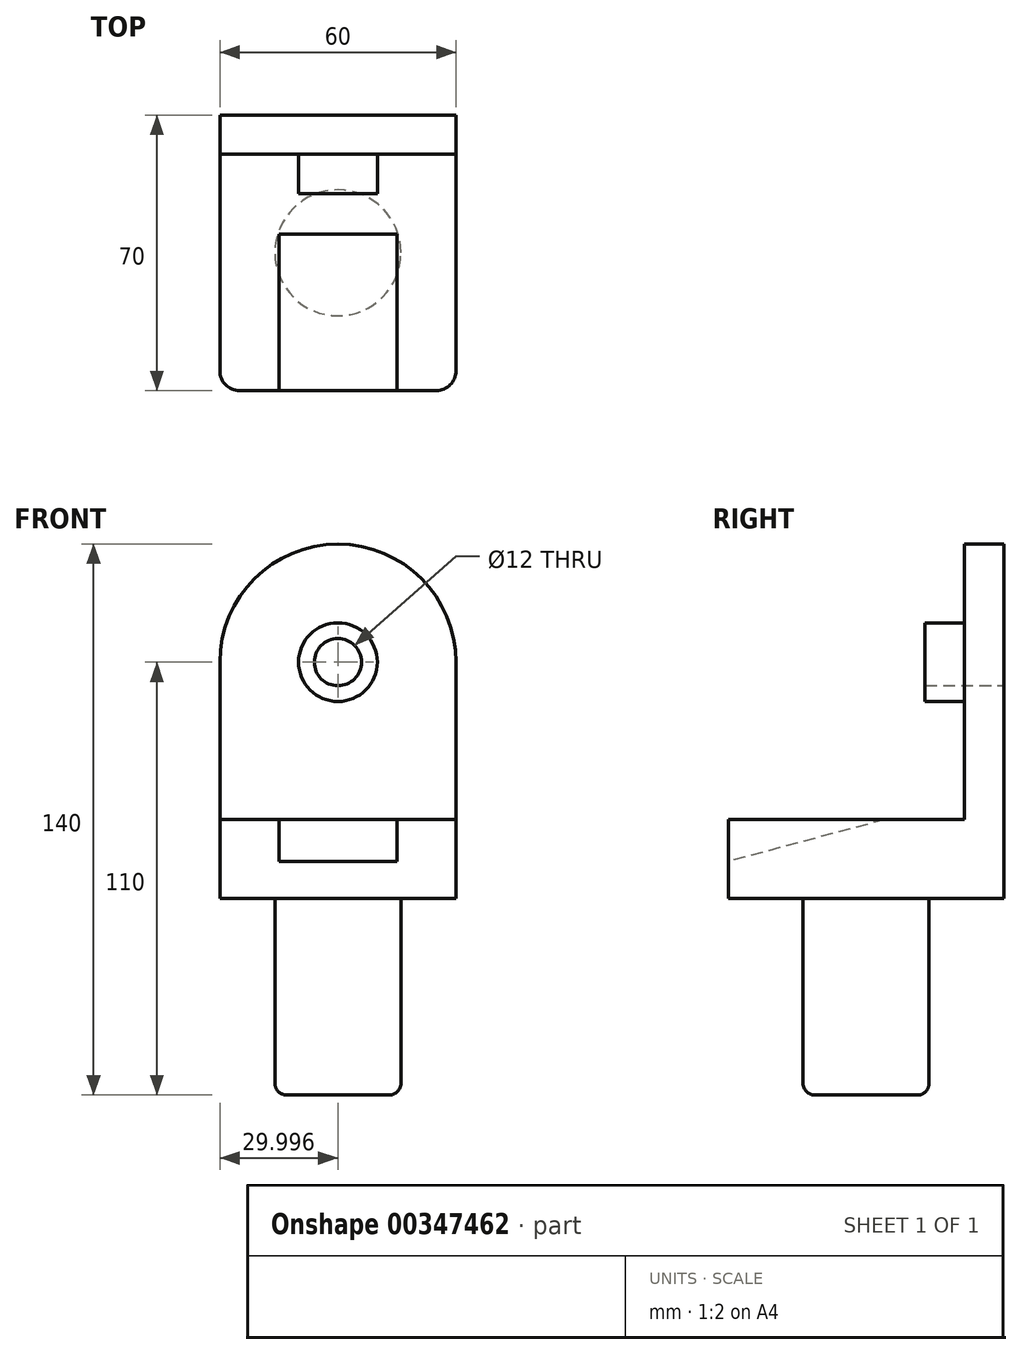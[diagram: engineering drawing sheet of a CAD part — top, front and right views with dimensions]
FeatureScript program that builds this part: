
annotation { "Feature Type Name" : "Feature", "Feature Type Description" : "" }
export const myFeature = defineFeature(function(context is Context, id is Id, definition is map)
    precondition{}
    {
        {
            var Q0;
            Q0=qCreatedBy(makeId("Top.planeOp"),FACE);
            var sketch = newSketch(context, id + "F0", { "sketchPlane" : qUnion([Q0])});
            skCircle(sketch, "E0", {"center": v(-41.77, 23.8) * mm, "radius": 16 * mm});
            skSolve(sketch);
        }
        {
            var Q0;
            Q0=makeQuery(id+"F0.imprint","IMPRINT",FACE,{"disambiguationData":[TD([[makeQuery(id+"F0.imprint","IMPRINT",EDGE,{"derivedFrom":sQuery(id+"F0.wireOp",EDGE,"E0")}),1.0]])]});
            extrude(context, id + "F1", {"entities" : qUnion([Q0]), "depth" : 50 * mm});
        }
        {
            var Q0;
            Q0=makeQuery(id+"F1.opExtrude","CAP_FACE",FACE,{"disambiguationData":[OSD([sQuery(id+"F0.wireOp",EDGE,"E0")])],"isStart":true});
            fillet(context, id + "F2", {"entities" : qUnion([Q0]), "radius" : 3 * mm, "tangentPropagation" : true, "allowEdgeOverflow" : false});
        }
        {
            var Q0;
            Q0=makeQuery(id+"F1.opExtrude","CAP_FACE",FACE,{"disambiguationData":[OSD([sQuery(id+"F0.wireOp",EDGE,"E0")])],"isStart":false});
            var sketch = newSketch(context, id + "F3", { "sketchPlane" : qUnion([Q0])});
            skLineSegment(sketch, "E1", {"start": v(-41.77, 58.8) * mm, "end": v(-71.77, 58.8) * mm});
            skLineSegment(sketch, "E2", {"start": v(-71.77, 58.8) * mm, "end": v(-71.77, 23.8) * mm});
            skLineSegment(sketch, "E3", {"start": v(-71.77, 23.8) * mm, "end": v(-71.77, -6.2) * mm});
            skLineSegment(sketch, "E4", {"start": v(-66.77, -11.2) * mm, "end": v(-16.77, -11.2) * mm});
            skLineSegment(sketch, "E5", {"start": v(-11.77, -6.2) * mm, "end": v(-11.77, 58.8) * mm});
            skLineSegment(sketch, "E6", {"start": v(-11.77, 58.8) * mm, "end": v(-41.77, 58.8) * mm});
            skPoint(sketch, "E7.visualSharp", {"position": v(-71.77, -11.2) * mm});
            skArc(sketch, "E7.filletArc", {"start": v(-71.77, -6.2) * mm, "mid": v(-70.3, -9.73) * mm, "end": v(-66.77, -11.2) * mm});
            skPoint(sketch, "E8.visualSharp", {"position": v(-11.77, -11.2) * mm});
            skArc(sketch, "E8.filletArc", {"start": v(-16.77, -11.2) * mm, "mid": v(-13.24, -9.73) * mm, "end": v(-11.77, -6.2) * mm});
            skLineSegment(sketch, "E9", {"start": v(-41.77, -11.2) * mm, "end": v(-56.77, -11.2) * mm});
            skLineSegment(sketch, "E10", {"start": v(-41.77, -11.2) * mm, "end": v(-26.77, -11.2) * mm});
            skSolve(sketch);
        }
        {
            var Q0;
            Q0=makeQuery(id+"F3.imprint","IMPRINT",FACE,{"disambiguationData":[TD([[makeQuery(id+"F3.imprint","IMPRINT",EDGE,{"derivedFrom":makeQuery(id+"F1.opExtrude","CAP_EDGE",EDGE,{"disambiguationData":[OSD([sQuery(id+"F0.wireOp",EDGE,"E0")])],"isStart":false})}),1.0]])]});
            var Q1;
            Q1=makeQuery(id+"F3.imprint","IMPRINT",FACE,{"disambiguationData":[TD([[makeQuery(id+"F3.imprint","IMPRINT",EDGE,{"derivedFrom":sQuery(id+"F3.wireOp",EDGE,"E1")}),1.0]])]});
            extrude(context, id + "F4", {"entities" : qUnion([Q0, Q1]), "operationType" : NewBodyOperationType.ADD, "depth" : 20 * mm});
        }
        {
            var Q0;
            Q0=makeQuery(id+"F4.opExtrude","SWEPT_FACE",FACE,{"disambiguationData":[OSD([sQuery(id+"F3.wireOp",EDGE,"E2"),sQuery(id+"F3.wireOp",EDGE,"E3")])]});
            cPlane(context, id + "F5", {"entities" : qUnion([Q0]), "cplaneType" : CPlaneType.OFFSET, "offset" : 30 * mm, "oppositeDirection" : true, "width" : 150 * mm, "height" : 150 * mm});
        }
        {
            var Q0;
            Q0=qCreatedBy(id+"F5.planeOp",FACE);
            var sketch = newSketch(context, id + "F6", { "sketchPlane" : qUnion([Q0])});
            skLineSegment(sketch, "E11", {"start": v(11.26, 70.05) * mm, "end": v(-28.74, 70.05) * mm});
            skLineSegment(sketch, "E12", {"start": v(-28.74, 70.05) * mm, "end": v(11.26, 59.33) * mm});
            skLineSegment(sketch, "E13", {"start": v(11.26, 59.33) * mm, "end": v(11.26, 70.05) * mm});
            skSolve(sketch);
        }
        {
            var Q0;
            Q0 = qSketchRegion(id + "F6", true);
            extrude(context, id + "F7", {"entities" : qUnion([Q0]), "operationType" : NewBodyOperationType.REMOVE, "endBound" : BoundingType.SYMMETRIC, "oppositeDirection" : true, "depth" : 30 * mm});
        }
        {
            var Q0;
            Q0=makeQuery(id+"F4.opExtrude","CAP_FACE",FACE,{"disambiguationData":[OSD([sQuery(id+"F3.wireOp",EDGE,"E1"),sQuery(id+"F3.wireOp",EDGE,"E2"),sQuery(id+"F3.wireOp",EDGE,"E3"),sQuery(id+"F3.wireOp",EDGE,"E4"),sQuery(id+"F3.wireOp",EDGE,"E5"),sQuery(id+"F3.wireOp",EDGE,"E6"),sQuery(id+"F3.wireOp",EDGE,"E7.filletArc"),sQuery(id+"F3.wireOp",EDGE,"E8.filletArc"),sQuery(id+"F3.wireOp",EDGE,"E9"),sQuery(id+"F3.wireOp",EDGE,"E10")])],"isStart":false});
            var sketch = newSketch(context, id + "F8", { "sketchPlane" : qUnion([Q0])});
            skLineSegment(sketch, "E14", {"start": v(-71.77, 58.8) * mm, "end": v(-71.77, 48.8) * mm});
            skLineSegment(sketch, "E15", {"start": v(-71.77, 48.8) * mm, "end": v(-11.77, 48.8) * mm});
            skLineSegment(sketch, "E16", {"start": v(-11.77, 48.8) * mm, "end": v(-11.77, 58.8) * mm});
            skLineSegment(sketch, "E17", {"start": v(-11.77, 58.8) * mm, "end": v(-71.77, 58.8) * mm});
            skSolve(sketch);
        }
        {
            var Q0;
            Q0=makeQuery(id+"F8.imprint","IMPRINT",FACE,{"disambiguationData":[TD([[makeQuery(id+"F8.imprint","IMPRINT",EDGE,{"derivedFrom":sQuery(id+"F8.wireOp",EDGE,"E14")}),1.0]])]});
            extrude(context, id + "F9", {"entities" : qUnion([Q0]), "operationType" : NewBodyOperationType.ADD, "depth" : 70 * mm});
        }
        {
            var Q0;
            Q0=makeQuery(id+"F9.opExtrude","CAP_EDGE",EDGE,{"disambiguationData":[OSD([sQuery(id+"F8.wireOp",EDGE,"E14")])],"isStart":false});
            var Q1;
            Q1=makeQuery(id+"F9.opExtrude","CAP_EDGE",EDGE,{"disambiguationData":[OSD([sQuery(id+"F8.wireOp",EDGE,"E16")])],"isStart":false});
            fillet(context, id + "F10", {"entities" : qUnion([Q0, Q1]), "radius" : 30 * mm, "tangentPropagation" : true, "allowEdgeOverflow" : false});
        }
        {
            var Q0;
            Q0=makeQuery(id+"F9.opExtrude","SWEPT_FACE",FACE,{"disambiguationData":[OSD([sQuery(id+"F8.wireOp",EDGE,"E15")])]});
            var sketch = newSketch(context, id + "F11", { "sketchPlane" : qUnion([Q0])});
            skCircle(sketch, "E18", {"center": v(-41.77, 110) * mm, "radius": 10 * mm});
            skCircle(sketch, "E19", {"center": v(-41.77, 110) * mm, "radius": 6 * mm});
            skSolve(sketch);
        }
        {
            var Q0;
            Q0=makeQuery(id+"F11.imprint","IMPRINT",FACE,{"disambiguationData":[TD([[makeQuery(id+"F11.imprint","IMPRINT",EDGE,{"derivedFrom":sQuery(id+"F11.wireOp",EDGE,"E18")}),1.0]])]});
            extrude(context, id + "F12", {"entities" : qUnion([Q0]), "operationType" : NewBodyOperationType.ADD, "depth" : 10 * mm});
        }
        {
            var Q0;
            Q0=makeQuery(id+"F12.boolean.opBoolean","SPLIT",FACE,{"disambiguationData":[TD([makeQuery(id+"F12.opExtrude","SWEPT_FACE",FACE,{"disambiguationData":[OSD([sQuery(id+"F11.wireOp",EDGE,"E19")])]})])],"derivedFrom":makeQuery(id+"F9.opExtrude","SWEPT_FACE",FACE,{"disambiguationData":[OSD([sQuery(id+"F8.wireOp",EDGE,"E15")])]})});
            extrude(context, id + "F13", {"entities" : qUnion([Q0]), "operationType" : NewBodyOperationType.REMOVE, "endBound" : BoundingType.THROUGH_ALL, "oppositeDirection" : true, "depth" : 25 * mm});
        }
    });
